# Revit family: Still
name_source: partatom
category: Furniture
revit_build: Autodesk Revit 2015 (Build: 20140606_1530(x64)
units: mm (PartAtom-declared; Revit-internal decimal feet)

## types (5) — shared parameters
Armrest materials = Plastic, Opaque Black
Manufacturer = Isku Oy
New still armrest = Yes
Plastic partsArmrest material = Plastic, Opaque Black
Still 29 backrest visibility = Yes
Type Comments = Available as antimicrobial
URL = www.isku.fi

## per-type parameters (varying)
| type | 3058 backrest visibility | Armrest | Backrest padding | Cloth hanger | Headrest | Headrest net back | Net backrest |
| Still S1A 3061 backsupport with net | No | Yes | No | No | No | Yes | Yes |
| Still 3058 (Still Light) | Yes | Yes | No | No | No | No | No |
| Still S1A 3061 | No | Yes | Yes | No | Yes | No | No |
| Still S1A 3061 with cloth hanger | No | Yes | Yes | Yes | Yes | No | No |
| Still 29 | No | No | No | No | No | Yes | No |

## geometry (parser evidence)
native form markers: Sweep x19
no freeform markers — native parametric forms only
